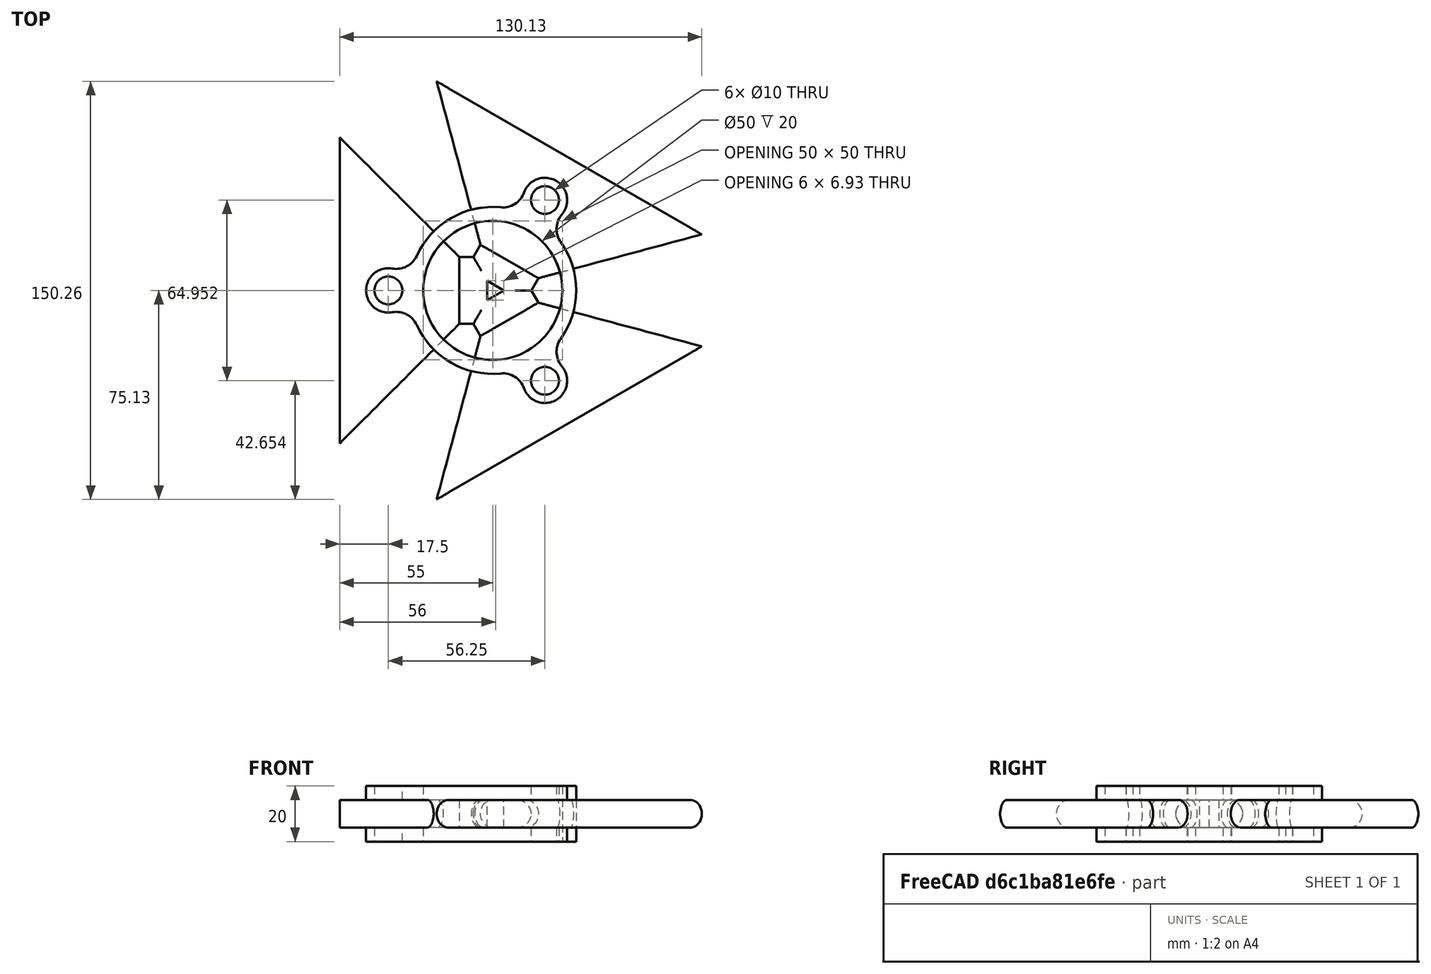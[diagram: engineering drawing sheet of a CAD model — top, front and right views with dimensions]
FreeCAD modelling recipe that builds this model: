
FCSTD DOCUMENT  (FreeCAD 1.0R39319 (Git))
Label: Mania2015-new
License: All rights reserved
LicenseURL: https://en.wikipedia.org/wiki/All_rights_reserved
objects: Sketcher::SketchObject×5, PartDesign::Pad×2, PartDesign::PolarPattern×2, PartDesign::Body×2, PartDesign::SubShapeBinder×1, PartDesign::AdditiveLoft×1, PartDesign::Boolean×1
note: 28 computed .brp shape members not serialized (recipe doc carries the construction recipe); baked Part::Feature solids carry a one-line shape summary decoded from their .brp

FEATURE [Sketcher::SketchObject] Sketch
  ArcFitTolerance = 1e-06
  AttachmentSupport = -> [XY_Plane]
  FullyConstrained = true
  MakeInternals = false
  MapMode = 5
  sketch-geometry (7):
    g0: Circle [constr] CenterX=0 CenterY=0 CenterZ=0 NormalX=0 NormalY=0 NormalZ=1 AngleXU=0 Radius=37.5
    g1: ArcOfCircle CenterX=0 CenterY=0 CenterZ=0 NormalX=0 NormalY=0 NormalZ=1 AngleXU=0 Radius=30 StartAngle=3.56847 EndAngle=8.9979
    g2: ArcOfCircle CenterX=-34.59 CenterY=15.7331 CenterZ=0 NormalX=0 NormalY=0 NormalZ=1 AngleXU=0 Radius=8 StartAngle=4.5295 EndAngle=5.85631
    g3: ArcOfCircle CenterX=-34.59 CenterY=-15.7331 CenterZ=0 NormalX=0 NormalY=0 NormalZ=1 AngleXU=0 Radius=8 StartAngle=0.426877 EndAngle=1.75369
    g4: ArcOfCircle CenterX=-37.5 CenterY=0 CenterZ=0 NormalX=0 NormalY=0 NormalZ=1 AngleXU=0 Radius=8 StartAngle=1.3879 EndAngle=4.89528
    g5: Circle CenterX=0 CenterY=0 CenterZ=0 NormalX=0 NormalY=0 NormalZ=1 AngleXU=0 Radius=25
    g6: Circle CenterX=-37.5 CenterY=0 CenterZ=0 NormalX=0 NormalY=0 NormalZ=1 AngleXU=0 Radius=5
  constraints (18):
    c: Diameter(g0) = 75
    c: Diameter(g1) = 60
    c: Coincident(g0,g-1)
    c: Coincident(g1,g0)
    c: Radius(g4) = 8
    c: Tangent(g4,g2) = 1.5708
    c: Tangent(g4,g3) = 1.5708
    c: Equal(g4,g2)
    c: Equal(g4,g3)
    c: PointOnObject(g4,g-1)
    c: PointOnObject(g4,g0)
    c: Tangent(g2,g1) = 1.5708
    c: Tangent(g3,g1) = 1.5708
    c: Diameter(g5) = 50
    c: Diameter(g6) = 10
    c: PointOnObject(g6,g-1)
    c: PointOnObject(g6,g0)
    c: Coincident(g5,g0)
FEATURE [PartDesign::Pad] Pad
  Direction = (0,0,1)
  Length = 20
  Length2 = 10
  Midplane = true
  Profile = -> Sketch
  ReferenceAxis = -> Sketch [N_Axis]
  Refine = true
  Suppressed = false
  Type = 0
FEATURE [Sketcher::SketchObject] Sketch001
  ArcFitTolerance = 1e-06
  AttachmentSupport = -> [XY_Plane]
  FullyConstrained = true
  MakeInternals = false
  MapMode = 5
  sketch-geometry (4):
    g0: LineSegment StartX=-55 StartY=55 StartZ=0 EndX=-55 EndY=-55 EndZ=0
    g1: LineSegment StartX=-55 StartY=-55 StartZ=0 EndX=-12 EndY=-12 EndZ=0
    g2: LineSegment StartX=-12 StartY=12 StartZ=0 EndX=-55 EndY=55 EndZ=0
    g3: LineSegment StartX=-12 StartY=12 StartZ=0 EndX=-12 EndY=-12 EndZ=0
  constraints (10):
    c: Coincident(g0,g1)
    c: Distance(g-2,g0) = 55
    c: Coincident(g2,g0)
    c: Angle(g2,g-1) = 0.785398
    c: Coincident(g3,g2)
    c: Coincident(g3,g1)
    c: Symmetric(g2,g1,g-1)
    c: DistanceY(g3,g3) = 24
    c: DistanceX(g2,g-1) = 12
    c: Symmetric(g0,g0,g-1)
FEATURE [PartDesign::SubShapeBinder] Binder001
  BindCopyOnChange = 0
  BindMode = 0
  ClaimChildren = false
  Context = -> Body [Boolean.Body001.Binder001.]
  Fuse = false
  MakeFace = true
  OffsetFill = false
  OffsetIntersection = false
  OffsetJoinType = 0
  OffsetOpenResult = false
  PartialLoad = false
  Refine = true
  Relative = true
  Support = -> [Body[Sketch001.]]
  _Version = 2
FEATURE [Sketcher::SketchObject] Sketch003
  ArcFitTolerance = 1e-06
  AttachmentOffset = pos=(0,0,-55) rot=(0,0,1;0rad)
  AttachmentSupport = -> [YZ_Plane001]
  ExternalGeometry = -> [Binder001]
  FullyConstrained = true
  MakeInternals = false
  MapMode = 5
  Placement = pos=(-55,0,0) rot=(0.57735,0.57735,0.57735;2.0944rad)
  sketch-geometry (4):
    g0: ArcOfCircle CenterX=-50 CenterY=0 CenterZ=0 NormalX=0 NormalY=0 NormalZ=1 AngleXU=0 Radius=5 StartAngle=1.5708 EndAngle=4.71239
    g1: ArcOfCircle CenterX=50 CenterY=0 CenterZ=0 NormalX=0 NormalY=0 NormalZ=1 AngleXU=0 Radius=5 StartAngle=4.71239 EndAngle=7.85398
    g2: LineSegment StartX=-50 StartY=5 StartZ=0 EndX=50 EndY=5 EndZ=0
    g3: LineSegment StartX=-50 StartY=-5 StartZ=0 EndX=50 EndY=-5 EndZ=0
  constraints (10):
    c: Tangent(g0,g2) = 1.5708
    c: Tangent(g0,g3) = -1.5708
    c: Tangent(g1,g2) = 1.5708
    c: Tangent(g1,g3) = -1.5708
    c: Equal(g0,g1)
    c: Radius(g1) = 5
    c: PointOnObject(g0,g-3)
    c: PointOnObject(g-3,g0)
    c: PointOnObject(g1,g-3)
    c: PointOnObject(g-3,g1)
FEATURE [Sketcher::SketchObject] Sketch004
  ArcFitTolerance = 1e-06
  FullyConstrained = true
  MakeInternals = false
  MapMode = 5
  Placement = pos=(-12,0,-5.3e-15) rot=(0.57735,0.57735,0.57735;2.0944rad)
  sketch-geometry (4):
    g0: ArcOfCircle CenterX=-7 CenterY=0 CenterZ=0 NormalX=0 NormalY=0 NormalZ=1 AngleXU=0 Radius=5 StartAngle=1.5708 EndAngle=4.71239
    g1: ArcOfCircle CenterX=7 CenterY=0 CenterZ=0 NormalX=0 NormalY=0 NormalZ=1 AngleXU=0 Radius=5 StartAngle=4.71239 EndAngle=7.85398
    g2: LineSegment StartX=-7 StartY=5 StartZ=0 EndX=7 EndY=5 EndZ=0
    g3: LineSegment StartX=-7 StartY=-5 StartZ=0 EndX=7 EndY=-5 EndZ=0
  constraints (10):
    c: Tangent(g0,g2) = 1.5708
    c: Tangent(g0,g3) = -1.5708
    c: Tangent(g1,g2) = 1.5708
    c: Tangent(g1,g3) = -1.5708
    c: Equal(g0,g1)
    c: Radius(g1) = 5
    c: PointOnObject(g1,g-1)
    c: PointOnObject(g0,g-1)
    c: PointOnObject(g-3,g1)
    c: PointOnObject(g-4,g0)
FEATURE [PartDesign::PolarPattern] PolarPattern
  Angle = 360
  Axis = -> Sketch [N_Axis]
  BaseFeature = -> Pad
  Mode = 0
  Occurrences = 3
  Offset = 120
  Originals = -> [Pad]
  Refine = true
  Suppressed = false
  TransformMode = 0
FEATURE [Sketcher::SketchObject] Sketch005
  ArcFitTolerance = 1e-06
  FullyConstrained = true
  MakeInternals = false
  MapMode = 5
  Placement = pos=(-12,0,-5.3e-15) rot=(0.57735,0.57735,0.57735;2.0944rad)
  sketch-geometry (4):
    g0: ArcOfCircle CenterX=-7 CenterY=0 CenterZ=0 NormalX=0 NormalY=0 NormalZ=1 AngleXU=0 Radius=5 StartAngle=1.5708 EndAngle=4.71239
    g1: ArcOfCircle CenterX=7 CenterY=0 CenterZ=0 NormalX=0 NormalY=0 NormalZ=1 AngleXU=0 Radius=5 StartAngle=4.71239 EndAngle=7.85398
    g2: LineSegment StartX=-7 StartY=5 StartZ=0 EndX=7 EndY=5 EndZ=0
    g3: LineSegment StartX=-7 StartY=-5 StartZ=0 EndX=7 EndY=-5 EndZ=0
  constraints (10):
    c: Tangent(g0,g2) = 1.5708
    c: Tangent(g0,g3) = -1.5708
    c: Tangent(g1,g2) = 1.5708
    c: Tangent(g1,g3) = -1.5708
    c: Equal(g0,g1)
    c: Radius(g1) = 5
    c: PointOnObject(g1,g-1)
    c: PointOnObject(g0,g-1)
    c: PointOnObject(g-3,g1)
    c: PointOnObject(g-4,g0)
FEATURE [PartDesign::AdditiveLoft] AdditiveLoft
  Closed = false
  Placement = pos=(-12,0,-5.3e-15) rot=(0.57735,0.57735,0.57735;2.0944rad)
  Profile = -> Sketch004
  Refine = true
  Ruled = false
  Sections = -> [Sketch003]
  Suppressed = false
FEATURE [PartDesign::Pad] Pad001
  BaseFeature = -> AdditiveLoft
  Direction = (1,1e-16,-1e-16)
  Length = 10
  Length2 = 10
  Placement = pos=(-12,0,-5.3e-15) rot=(0.57735,0.57735,0.57735;2.0944rad)
  Profile = -> Sketch005
  ReferenceAxis = -> Sketch005 [N_Axis]
  Refine = true
  Suppressed = false
  Type = 0
FEATURE [PartDesign::PolarPattern] PolarPattern001
  Angle = 360
  Axis = -> Z_Axis001
  BaseFeature = -> Pad001
  Mode = 0
  Occurrences = 3
  Offset = 120
  Originals = -> [Pad001]
  Placement = pos=(-12,0,-5.3e-15) rot=(0.57735,0.57735,0.57735;2.0944rad)
  Refine = true
  Suppressed = false
  TransformMode = 1
FEATURE [PartDesign::Body] Body001
  AllowCompound = false
  Group = -> [Binder001,Sketch003,Sketch004,Sketch005,AdditiveLoft,Pad001,PolarPattern001]
  Origin = -> Origin001
  Tip = -> PolarPattern001
FEATURE [PartDesign::Boolean] Boolean
  BaseFeature = -> PolarPattern
  Group = -> [Body001]
  Refine = true
  Suppressed = false
  Type = 1
  UsePlacement = true
FEATURE [PartDesign::Body] Body
  AllowCompound = false
  Group = -> [Sketch,Pad,Sketch001,PolarPattern,Boolean]
  Origin = -> Origin
  Tip = -> Boolean
